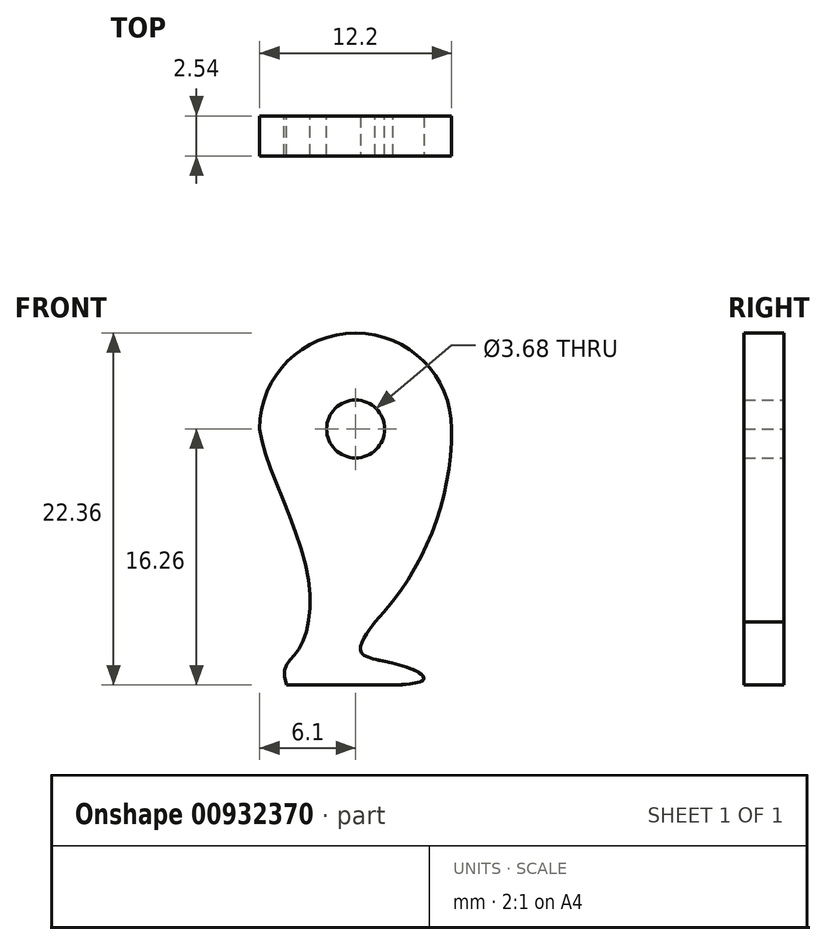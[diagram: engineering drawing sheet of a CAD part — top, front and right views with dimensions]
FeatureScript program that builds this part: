
annotation { "Feature Type Name" : "Feature", "Feature Type Description" : "" }
export const myFeature = defineFeature(function(context is Context, id is Id, definition is map)
    precondition{}
    {
        {
            var Q0;
            Q0=qCreatedBy(makeId("Front.planeOp"),FACE);
            var sketch = newSketch(context, id + "F0", { "sketchPlane" : qUnion([Q0])});
            skArc(sketch, "E0", {"start": v(6.1, 0) * mm, "mid": v(0, 6.1) * mm, "end": v(-6.1, 0) * mm});
            skCircle(sketch, "E1", {"center": v(0, 0) * mm, "radius": 1.84 * mm});
            skFitSpline(sketch, "E2", {"points": [v(-6.1, 0) * mm, v(-3.1, -9) * mm, v(-3.68, -14.1) * mm, v(-4.53, -15.35) * mm, v(-4.4, -16.26) * mm], "startDerivative": vector(1.88, -16.21) * mm, "endDerivative": vector(0, 0) * mm});
            skLineSegment(sketch, "E3", {"start": v(-4.4, -16.26) * mm, "end": v(2.37, -16.26) * mm});
            skArc(sketch, "E4", {"start": v(6.1, 0) * mm, "mid": v(4.84, -6.6) * mm, "end": v(1.23, -12.26) * mm});
            skFitSpline(sketch, "E5", {"points": [v(1.23, -12.26) * mm, v(0.3, -14.1) * mm, v(3.5, -15.22) * mm, v(2.37, -16.26) * mm], "startDerivative": vector(-3.25, -4.64) * mm, "endDerivative": vector(-30.88, -0.5) * mm});
            skSolve(sketch);
        }
        {
            var Q0;
            Q0=makeQuery(id+"F0.imprint","IMPRINT",FACE,{"disambiguationData":[TD([[makeQuery(id+"F0.imprint","IMPRINT",EDGE,{"derivedFrom":sQuery(id+"F0.wireOp",EDGE,"E0")}),1.0]])]});
            extrude(context, id + "F1", {"entities" : qUnion([Q0]), "depth" : 2.54 * mm, "offsetDistance" : 25 * mm});
        }
    });
